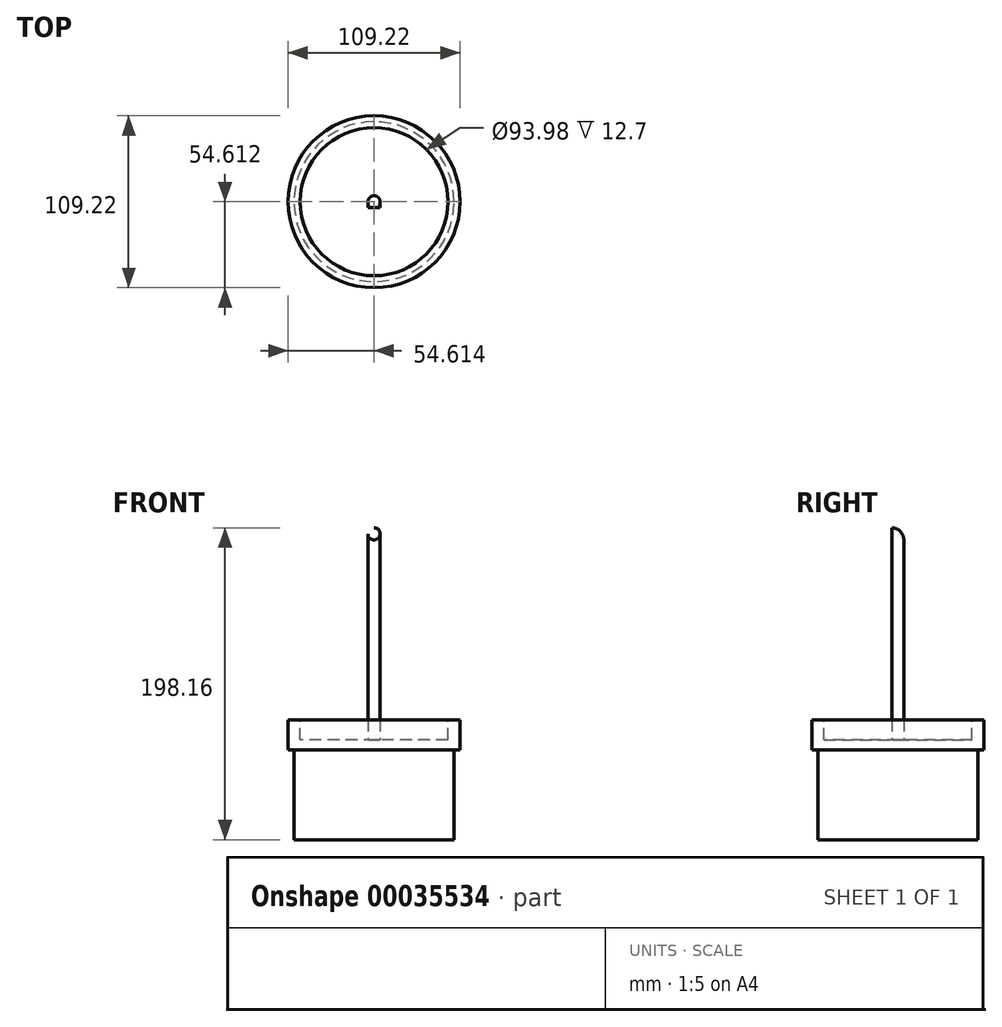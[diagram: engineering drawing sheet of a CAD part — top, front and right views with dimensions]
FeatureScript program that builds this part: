
annotation { "Feature Type Name" : "Feature", "Feature Type Description" : "" }
export const myFeature = defineFeature(function(context is Context, id is Id, definition is map)
    precondition{}
    {
        {
            var Q0;
            Q0=qCreatedBy(makeId("Top.planeOp"),FACE);
            var sketch = newSketch(context, id + "F0", { "sketchPlane" : qUnion([Q0])});
            skCircle(sketch, "E0", {"center": v(-17.56, 6.96) * mm, "radius": 50.8 * mm});
            skSolve(sketch);
        }
        {
            var Q0;
            Q0 = qSketchRegion(id + "F0", true);
            extrude(context, id + "F1", {"entities" : qUnion([Q0]), "depth" : 76.2 * mm});
        }
        {
            var Q0;
            Q0=makeQuery(id+"F1.opExtrude","CAP_FACE",FACE,{"disambiguationData":[OSD([sQuery(id+"F0.wireOp",EDGE,"E0")])],"isStart":false});
            var sketch = newSketch(context, id + "F2", { "sketchPlane" : qUnion([Q0])});
            skCircle(sketch, "E1", {"center": v(-17.56, 6.96) * mm, "radius": 54.61 * mm});
            skSolve(sketch);
        }
        {
            var Q0;
            Q0 = qSketchRegion(id + "F2", true);
            extrude(context, id + "F3", {"entities" : qUnion([Q0]), "operationType" : NewBodyOperationType.ADD, "oppositeDirection" : true, "depth" : 19.05 * mm});
        }
        {
            var Q0;
            Q0=makeQuery(id+"F3.boolean.opBoolean","MERGE",FACE,{"derivedFrom":[makeQuery(id+"F1.opExtrude","CAP_FACE",FACE,{"disambiguationData":[OSD([sQuery(id+"F0.wireOp",EDGE,"E0")])],"isStart":false}),makeQuery(id+"F3.opExtrude","CAP_FACE",FACE,{"disambiguationData":[OSD([sQuery(id+"F2.wireOp",EDGE,"E1")])],"isStart":true})]});
            var sketch = newSketch(context, id + "F4", { "sketchPlane" : qUnion([Q0])});
            skCircle(sketch, "E2", {"center": v(-17.56, 6.96) * mm, "radius": 47 * mm});
            skSolve(sketch);
        }
        {
            var Q0;
            Q0 = qSketchRegion(id + "F4", true);
            extrude(context, id + "F5", {"entities" : qUnion([Q0]), "operationType" : NewBodyOperationType.REMOVE, "oppositeDirection" : true, "depth" : 12.7 * mm});
        }
        {
            var Q0;
            Q0=makeQuery(id+"F5.boolean.opBoolean","COPY",FACE,{"derivedFrom":makeQuery(id+"F5.opExtrude","CAP_FACE",FACE,{"disambiguationData":[OSD([sQuery(id+"F4.wireOp",EDGE,"E2")])],"isStart":false})});
            var sketch = newSketch(context, id + "F6", { "sketchPlane" : qUnion([Q0])});
            skCircle(sketch, "E3", {"center": v(-17.56, 6.96) * mm, "radius": 3.83 * mm});
            skSolve(sketch);
        }
        {
            var Q0;
            Q0=makeQuery(id+"F6.imprint","IMPRINT",FACE,{"disambiguationData":[TD([[makeQuery(id+"F6.imprint","IMPRINT",EDGE,{"derivedFrom":sQuery(id+"F6.wireOp",EDGE,"E3")}),1.0]])]});
            extrude(context, id + "F7", {"entities" : qUnion([Q0]), "depth" : 127 * mm});
        }
        {
            var Q0;
            Q0=makeQuery(id+"F7.opExtrude","CAP_FACE",FACE,{"disambiguationData":[OSD([sQuery(id+"F6.wireOp",EDGE,"E3")])],"isStart":false});
            var sketch = newSketch(context, id + "F8", { "sketchPlane" : qUnion([Q0])});
            skLineSegment(sketch, "E4", {"start": v(-17.57, 3.13) * mm, "end": v(-3.43, 3.1) * mm});
            skLineSegment(sketch, "E5", {"start": v(-3.43, 3.1) * mm, "end": v(-32.09, 3.17) * mm});
            skSolve(sketch);
        }
        {
            var Q0;
            Q0=makeQuery(id+"F8.imprint","IMPRINT",FACE,{"disambiguationData":[TD([[makeQuery(id+"F8.imprint","IMPRINT",EDGE,{"derivedFrom":makeQuery(id+"F7.opExtrude","CAP_EDGE",EDGE,{"disambiguationData":[OSD([sQuery(id+"F6.wireOp",EDGE,"E3")])],"isStart":false})}),1.0]])]});
            var Q1;
            Q1=sQuery(id+"F8.wireOp",EDGE,"E5");
            revolve(context, id + "F9", {"operationType" : NewBodyOperationType.ADD, "entities" : qUnion([Q0]), "axis" : qUnion([Q1]), "revolveType" : RevolveType.ONE_DIRECTION, "oppositeDirection" : true, "angle" : 90 * degree});
        }
    });
